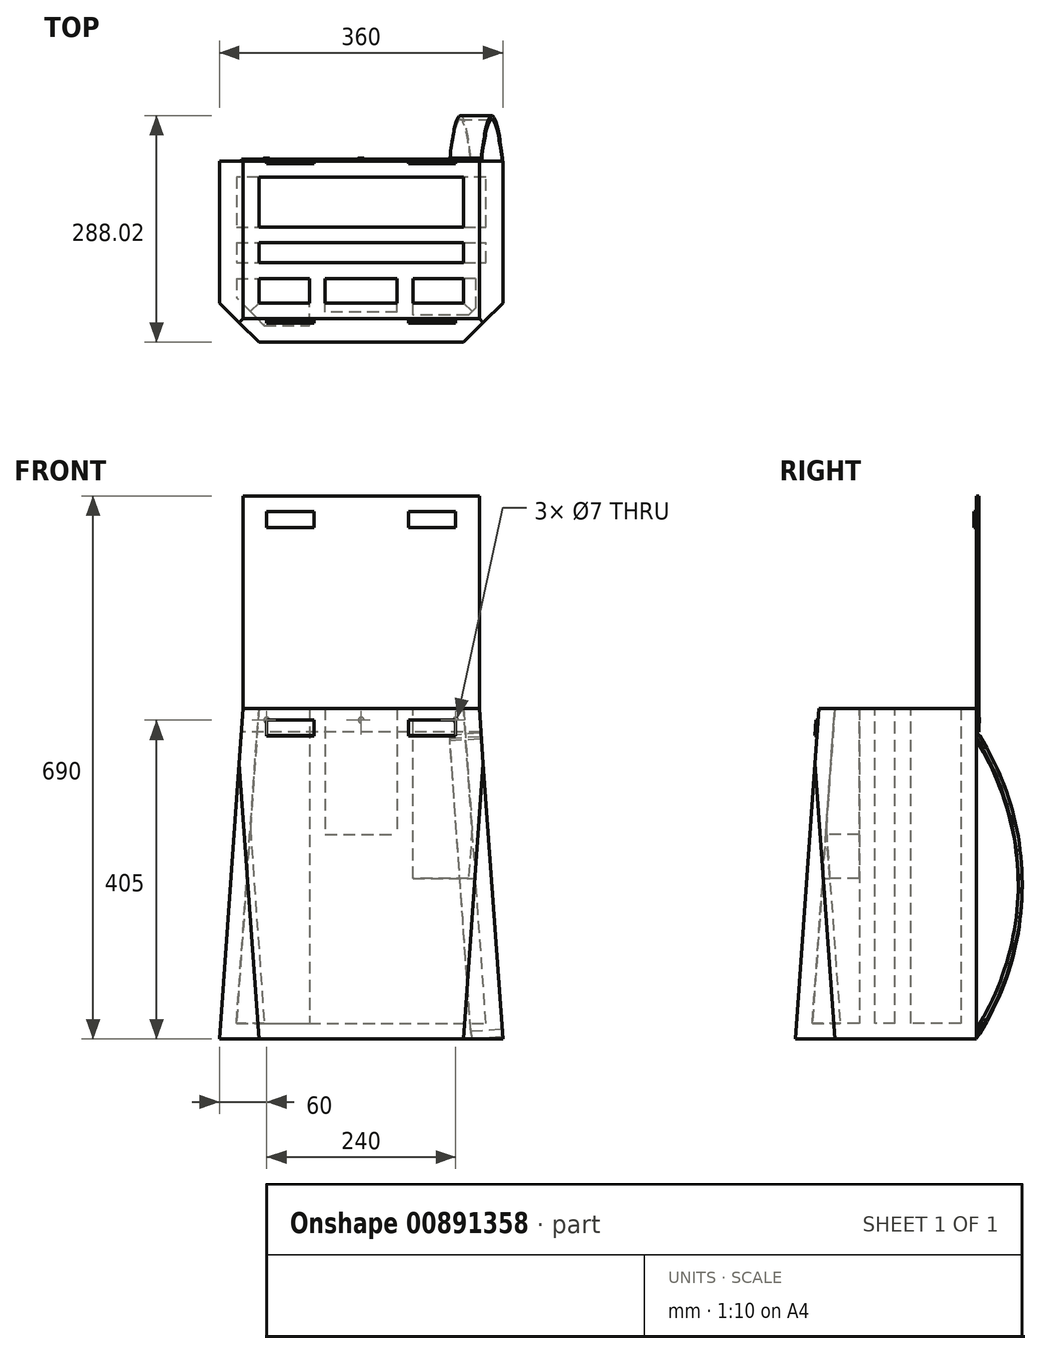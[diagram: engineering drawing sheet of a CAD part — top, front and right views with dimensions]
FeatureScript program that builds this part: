
annotation { "Feature Type Name" : "Feature", "Feature Type Description" : "" }
export const myFeature = defineFeature(function(context is Context, id is Id, definition is map)
    precondition{}
    {
        {
            var Q0;
            Q0=qCreatedBy(makeId("Top.planeOp"),FACE);
            var sketch = newSketch(context, id + "F0", { "sketchPlane" : qUnion([Q0])});
            skLineSegment(sketch, "E0.bottom", {"start": v(150, 100) * mm, "end": v(-150, 100) * mm});
            skLineSegment(sketch, "E0.top", {"start": v(150, -100) * mm, "end": v(-150, -100) * mm});
            skLineSegment(sketch, "E0.left", {"start": v(150, 100) * mm, "end": v(150, -100) * mm});
            skLineSegment(sketch, "E0.right", {"start": v(-150, 100) * mm, "end": v(-150, -100) * mm});
            skPoint(sketch, "E0.middle", {"position": v(0, 0) * mm});
            skSolve(sketch);
        }
        {
            var Q0;
            Q0 = qSketchRegion(id + "F0", true);
            extrude(context, id + "F1", {"entities" : qUnion([Q0]), "depth" : 420 * mm, "offsetDistance" : 25 * mm});
        }
        {
            var Q0;
            Q0=makeQuery(id+"F1.opExtrude","CAP_FACE",FACE,{"disambiguationData":[OSD([sQuery(id+"F0.wireOp",EDGE,"E0.bottom"),sQuery(id+"F0.wireOp",EDGE,"E0.top"),sQuery(id+"F0.wireOp",EDGE,"E0.left"),sQuery(id+"F0.wireOp",EDGE,"E0.right")])],"isStart":true});
            var sketch = newSketch(context, id + "F2", { "sketchPlane" : qUnion([Q0])});
            skLineSegment(sketch, "E1", {"start": v(-150, -100) * mm, "end": v(-180, -100) * mm});
            skLineSegment(sketch, "E2", {"start": v(180, 130) * mm, "end": v(180, -100) * mm});
            skLineSegment(sketch, "E3", {"start": v(180, -100) * mm, "end": v(150, -100) * mm});
            skLineSegment(sketch, "E4", {"start": v(-180, -100) * mm, "end": v(-180, 130) * mm});
            skLineSegment(sketch, "E5", {"start": v(-180, 130) * mm, "end": v(180, 130) * mm});
            skSolve(sketch);
        }
        {
            var Q0;
            Q0=makeQuery(id+"F2.imprint","IMPRINT",FACE,{"disambiguationData":[TD([[makeQuery(id+"F2.imprint","IMPRINT",EDGE,{"derivedFrom":sQuery(id+"F2.wireOp",EDGE,"E1")}),-1.0]])]});
            extrude(context, id + "F3", {"entities" : qUnion([Q0]), "operationType" : NewBodyOperationType.ADD, "oppositeDirection" : true, "depth" : 420 * mm, "offsetDistance" : 25 * mm});
        }
        {
            var Q0;
            Q0=makeQuery(id+"F3.opExtrude","SWEPT_FACE",FACE,{"disambiguationData":[OSD([sQuery(id+"F2.wireOp",EDGE,"E2")])]});
            var sketch = newSketch(context, id + "F4", { "sketchPlane" : qUnion([Q0])});
            skLineSegment(sketch, "E6", {"start": v(-100, 420) * mm, "end": v(-130, 0) * mm});
            skSolve(sketch);
        }
        {
            var Q0;
            {var subQ0=sQuery(id+"F4.wireOp",EDGE,"E6");Q0=makeQuery(id+"F4.imprint","IMPRINT",FACE,{"disambiguationData":[TD([[makeQuery(id+"F4.imprint","IMPRINT",EDGE,{"derivedFrom":subQ0}),-1.0]])]});}
            extrude(context, id + "F5", {"entities" : qUnion([Q0]), "operationType" : NewBodyOperationType.REMOVE, "endBound" : BoundingType.UP_TO_NEXT, "oppositeDirection" : true, "depth" : 25 * mm, "offsetDistance" : 25 * mm});
        }
        {
            var Q0;
            Q0=makeQuery(id+"F3.boolean.opBoolean","MERGE",FACE,{"derivedFrom":[makeQuery(id+"F1.opExtrude","SWEPT_FACE",FACE,{"disambiguationData":[OSD([sQuery(id+"F0.wireOp",EDGE,"E0.bottom")])]}),makeQuery(id+"F3.opExtrude","SWEPT_FACE",FACE,{"disambiguationData":[OSD([sQuery(id+"F2.wireOp",EDGE,"E1")])]}),makeQuery(id+"F3.opExtrude","SWEPT_FACE",FACE,{"disambiguationData":[OSD([sQuery(id+"F2.wireOp",EDGE,"E3")])]})]});
            var sketch = newSketch(context, id + "F6", { "sketchPlane" : qUnion([Q0])});
            skLineSegment(sketch, "E7", {"start": v(-150, 420) * mm, "end": v(-180, 0) * mm});
            skLineSegment(sketch, "E8", {"start": v(150, 420) * mm, "end": v(180, 0) * mm});
            skSolve(sketch);
        }
        {
            var Q0;
            Q0 = qSketchRegion(id + "F6", true);
            var Q1;
            {var subQ0=sQuery(id+"F6.wireOp",EDGE,"E7");Q1=makeQuery(id+"F6.imprint","IMPRINT",FACE,{"disambiguationData":[TD([[makeQuery(id+"F6.imprint","IMPRINT",EDGE,{"derivedFrom":subQ0}),-1.0]])]});}
            var Q2;
            {var subQ0=sQuery(id+"F6.wireOp",EDGE,"E8");Q2=makeQuery(id+"F6.imprint","IMPRINT",FACE,{"disambiguationData":[TD([[makeQuery(id+"F6.imprint","IMPRINT",EDGE,{"derivedFrom":subQ0}),1.0]])]});}
            extrude(context, id + "F7", {"entities" : qUnion([Q0, Q1, Q2]), "operationType" : NewBodyOperationType.REMOVE, "endBound" : BoundingType.UP_TO_NEXT, "oppositeDirection" : true, "depth" : 25 * mm, "offsetDistance" : 25 * mm});
        }
        {
            var Q0;
            {var subQ0=sQuery(id+"F0.wireOp",EDGE,"E0.right");var subQ1=sQuery(id+"F0.wireOp",EDGE,"E0.left");var subQ2=sQuery(id+"F0.wireOp",EDGE,"E0.top");Q0=makeQuery(id+"F3.boolean.opBoolean","MERGE",FACE,{"derivedFrom":[makeQuery(id+"F1.opExtrude","CAP_FACE",FACE,{"disambiguationData":[OSD([sQuery(id+"F0.wireOp",EDGE,"E0.bottom"),subQ2,subQ1,subQ0])],"isStart":true}),makeQuery(id+"F3.opExtrude","CAP_FACE",FACE,{"disambiguationData":[OSD([subQ2,subQ1,subQ0,sQuery(id+"F2.wireOp",EDGE,"E1"),sQuery(id+"F2.wireOp",EDGE,"E2"),sQuery(id+"F2.wireOp",EDGE,"E3"),sQuery(id+"F2.wireOp",EDGE,"E4"),sQuery(id+"F2.wireOp",EDGE,"E5")])],"isStart":true})]});}
            var sketch = newSketch(context, id + "F8", { "sketchPlane" : qUnion([Q0])});
            skLineSegment(sketch, "E9", {"start": v(-130, 130) * mm, "end": v(-180, 80) * mm});
            skLineSegment(sketch, "E10", {"start": v(130, 130) * mm, "end": v(180, 80) * mm});
            skSolve(sketch);
        }
        {
            var Q0;
            Q0 = qSketchRegion(id + "F8", true);
            var Q1;
            {var subQ0=sQuery(id+"F8.wireOp",EDGE,"E9");Q1=makeQuery(id+"F8.imprint","IMPRINT",FACE,{"disambiguationData":[TD([[makeQuery(id+"F8.imprint","IMPRINT",EDGE,{"derivedFrom":subQ0}),-1.0]])]});}
            var Q2;
            {var subQ0=sQuery(id+"F8.wireOp",EDGE,"E10");Q2=makeQuery(id+"F8.imprint","IMPRINT",FACE,{"disambiguationData":[TD([[makeQuery(id+"F8.imprint","IMPRINT",EDGE,{"derivedFrom":subQ0}),1.0]])]});}
            extrude(context, id + "F9", {"entities" : qUnion([Q0, Q1, Q2]), "operationType" : NewBodyOperationType.REMOVE, "oppositeDirection" : true, "depth" : 1000 * mm, "offsetDistance" : 25 * mm});
        }
        {
            var Q0;
            {var subQ0=sQuery(id+"F0.wireOp",EDGE,"E0.right");var subQ1=sQuery(id+"F0.wireOp",EDGE,"E0.left");var subQ2=sQuery(id+"F0.wireOp",EDGE,"E0.top");Q0=makeQuery(id+"F3.boolean.opBoolean","MERGE",FACE,{"derivedFrom":[makeQuery(id+"F1.opExtrude","CAP_FACE",FACE,{"disambiguationData":[OSD([sQuery(id+"F0.wireOp",EDGE,"E0.bottom"),subQ2,subQ1,subQ0])],"isStart":false}),makeQuery(id+"F3.opExtrude","CAP_FACE",FACE,{"disambiguationData":[OSD([subQ2,subQ1,subQ0,sQuery(id+"F2.wireOp",EDGE,"E1"),sQuery(id+"F2.wireOp",EDGE,"E2"),sQuery(id+"F2.wireOp",EDGE,"E3"),sQuery(id+"F2.wireOp",EDGE,"E4"),sQuery(id+"F2.wireOp",EDGE,"E5")])],"isStart":false})]});}
            shell(context, id + "F10", {"entities" : qUnion([Q0]), "thickness" : 20 * mm});
        }
        {
            var Q0;
            Q0=makeQuery(id+"F10.opShell","OFFSET_FACE",FACE,{"disambiguationData":[OSD([sQuery(id+"F0.wireOp",EDGE,"E0.bottom"),sQuery(id+"F0.wireOp",EDGE,"E0.top"),sQuery(id+"F0.wireOp",EDGE,"E0.left"),sQuery(id+"F0.wireOp",EDGE,"E0.right"),sQuery(id+"F2.wireOp",EDGE,"E1"),sQuery(id+"F2.wireOp",EDGE,"E2"),sQuery(id+"F2.wireOp",EDGE,"E3"),sQuery(id+"F2.wireOp",EDGE,"E4"),sQuery(id+"F2.wireOp",EDGE,"E5")])]});
            var sketch = newSketch(context, id + "F11", { "sketchPlane" : qUnion([Q0])});
            skLineSegment(sketch, "E11.bottom", {"start": v(-158.52, 80) * mm, "end": v(158.52, 80) * mm});
            skLineSegment(sketch, "E11.top", {"start": v(-158.52, 16.5) * mm, "end": v(158.52, 16.5) * mm});
            skLineSegment(sketch, "E11.left", {"start": v(-158.52, 80) * mm, "end": v(-158.52, 16.5) * mm});
            skLineSegment(sketch, "E11.right", {"start": v(158.52, 80) * mm, "end": v(158.52, 16.5) * mm});
            skLineSegment(sketch, "E12.bottom", {"start": v(-158.52, -3.5) * mm, "end": v(158.52, -3.5) * mm});
            skLineSegment(sketch, "E12.top", {"start": v(-158.52, -28.9) * mm, "end": v(158.52, -28.9) * mm});
            skLineSegment(sketch, "E12.left", {"start": v(-158.52, -3.5) * mm, "end": v(-158.52, -28.9) * mm});
            skLineSegment(sketch, "E12.right", {"start": v(158.52, -3.5) * mm, "end": v(158.52, -28.9) * mm});
            skLineSegment(sketch, "E13", {"start": v(-65.62, -48.9) * mm, "end": v(-65.62, -83.52) * mm});
            skLineSegment(sketch, "E14", {"start": v(65.62, -48.9) * mm, "end": v(65.62, -83.52) * mm});
            skPoint(sketch, "E14.endSnap0", {"position": v(0, -108.52) * mm});
            skLineSegment(sketch, "E15", {"start": v(-158.52, -48.9) * mm, "end": v(158.52, -48.9) * mm});
            skLineSegment(sketch, "E16", {"start": v(158.52, -48.9) * mm, "end": v(158.52, -83.52) * mm});
            skLineSegment(sketch, "E17", {"start": v(45.62, -48.9) * mm, "end": v(45.62, -83.52) * mm});
            skLineSegment(sketch, "E18", {"start": v(-45.62, -48.9) * mm, "end": v(-45.62, -83.52) * mm});
            skPoint(sketch, "E19.orphan", {"position": v(65.62, -108.52) * mm});
            skLineSegment(sketch, "E20", {"start": v(-45.62, -83.52) * mm, "end": v(-45.62, -108.52) * mm});
            skLineSegment(sketch, "E21", {"start": v(-65.62, -83.52) * mm, "end": v(-65.62, -108.52) * mm});
            skLineSegment(sketch, "E22", {"start": v(45.62, -83.52) * mm, "end": v(45.62, -108.52) * mm});
            skLineSegment(sketch, "E23", {"start": v(45.62, -108.52) * mm, "end": v(46.06, -113.28) * mm});
            skLineSegment(sketch, "E24", {"start": v(65.62, -83.52) * mm, "end": v(65.62, -108.52) * mm});
            skSolve(sketch);
        }
        {
            var Q0;
            {var subQ0=sQuery(id+"F11.wireOp",EDGE,"E11.top");Q0=makeQuery(id+"F11.imprint","IMPRINT",FACE,{"disambiguationData":[TD([[makeQuery(id+"F11.imprint","IMPRINT",EDGE,{"derivedFrom":subQ0}),-1.0]])]});}
            extrude(context, id + "F12", {"entities" : qUnion([Q0]), "operationType" : NewBodyOperationType.ADD, "depth" : 400 * mm, "offsetDistance" : 25 * mm});
        }
        {
            var Q0;
            {var subQ0=sQuery(id+"F11.wireOp",EDGE,"E12.bottom");var subQ1=sQuery(id+"F6.wireOp",EDGE,"E8");Q0=makeQuery(id+"F12.boolean.opBoolean","SPLIT",FACE,{"disambiguationData":[TD([makeQuery(id+"F7.boolean.opBoolean","COPY",FACE,{"derivedFrom":makeQuery(id+"F7.opExtrude","SWEPT_FACE",FACE,{"disambiguationData":[OSD([subQ1])]})})])],"derivedFrom":makeQuery(id+"F12.opExtrude","SWEPT_FACE",FACE,{"disambiguationData":[OSD([subQ0])]})});}
            extrude(context, id + "F13", {"entities" : qUnion([Q0]), "operationType" : NewBodyOperationType.REMOVE, "oppositeDirection" : true, "depth" : 25 * mm, "offsetDistance" : 25 * mm});
        }
        {
            var Q0;
            {var subQ0=sQuery(id+"F11.wireOp",EDGE,"E12.bottom");Q0=makeQuery(id+"F12.boolean.opBoolean","SPLIT",FACE,{"disambiguationData":[TD([makeQuery(id+"F7.boolean.opBoolean","COPY",FACE,{"derivedFrom":makeQuery(id+"F7.opExtrude","SWEPT_FACE",FACE,{"disambiguationData":[OSD([sQuery(id+"F6.wireOp",EDGE,"E7")])]})})])],"derivedFrom":makeQuery(id+"F12.opExtrude","SWEPT_FACE",FACE,{"disambiguationData":[OSD([subQ0])]})});}
            extrude(context, id + "F14", {"entities" : qUnion([Q0]), "operationType" : NewBodyOperationType.REMOVE, "oppositeDirection" : true, "depth" : 25 * mm, "offsetDistance" : 25 * mm});
        }
        {
            var Q0;
            {var subQ7=sQuery(id+"F11.wireOp",EDGE,"E12.top");Q0=makeQuery(id+"F11.imprint","IMPRINT",FACE,{"disambiguationData":[TD([[makeQuery(id+"F11.imprint","IMPRINT",EDGE,{"derivedFrom":subQ7}),-1.0]])]});}
            extrude(context, id + "F15", {"entities" : qUnion([Q0]), "operationType" : NewBodyOperationType.ADD, "depth" : 400 * mm, "offsetDistance" : 25 * mm});
        }
        {
            var Q0;
            {var subQ0=sQuery(id+"F11.wireOp",EDGE,"E13");Q0=makeQuery(id+"F11.imprint","IMPRINT",FACE,{"disambiguationData":[TD([[makeQuery(id+"F11.imprint","IMPRINT",EDGE,{"derivedFrom":subQ0}),1.0]])]});}
            var Q1;
            {var subQ0=sQuery(id+"F11.wireOp",EDGE,"E14");Q1=makeQuery(id+"F11.imprint","IMPRINT",FACE,{"disambiguationData":[TD([[makeQuery(id+"F11.imprint","IMPRINT",EDGE,{"derivedFrom":subQ0}),-1.0]])]});}
            extrude(context, id + "F16", {"entities" : qUnion([Q0, Q1]), "operationType" : NewBodyOperationType.ADD, "depth" : 400 * mm, "offsetDistance" : 25 * mm});
        }
        {
            var Q0;
            {var subQ0=sQuery(id+"F6.wireOp",EDGE,"E8");var subQ11=sQuery(id+"F11.wireOp",EDGE,"E15");Q0=makeQuery(id+"F15.boolean.opBoolean","SPLIT",FACE,{"disambiguationData":[TD([makeQuery(id+"F7.boolean.opBoolean","COPY",FACE,{"derivedFrom":makeQuery(id+"F7.opExtrude","SWEPT_FACE",FACE,{"disambiguationData":[OSD([subQ0])]})})])],"derivedFrom":makeQuery(id+"F15.opExtrude","SWEPT_FACE",FACE,{"disambiguationData":[OSD([subQ11])]})});}
            var Q1;
            {var subQ11=sQuery(id+"F11.wireOp",EDGE,"E15");Q1=makeQuery(id+"F15.boolean.opBoolean","SPLIT",FACE,{"disambiguationData":[TD([makeQuery(id+"F7.boolean.opBoolean","COPY",FACE,{"derivedFrom":makeQuery(id+"F7.opExtrude","SWEPT_FACE",FACE,{"disambiguationData":[OSD([sQuery(id+"F6.wireOp",EDGE,"E7")])]})})])],"derivedFrom":makeQuery(id+"F15.opExtrude","SWEPT_FACE",FACE,{"disambiguationData":[OSD([subQ11])]})});}
            extrude(context, id + "F17", {"entities" : qUnion([Q0, Q1]), "operationType" : NewBodyOperationType.REMOVE, "oppositeDirection" : true, "depth" : 25 * mm, "offsetDistance" : 25 * mm});
        }
        {
            var Q0;
            {var subQ1=sQuery(id+"F4.wireOp",EDGE,"E6");var subQ12=sQuery(id+"F11.wireOp",EDGE,"E21");var subQ14=sQuery(id+"F11.wireOp",EDGE,"E13");Q0=makeQuery(id+"F16.boolean.opBoolean","SPLIT",FACE,{"disambiguationData":[TD([makeQuery(id+"F5.boolean.opBoolean","COPY",FACE,{"derivedFrom":makeQuery(id+"F5.opExtrude","SWEPT_FACE",FACE,{"disambiguationData":[OSD([subQ1])]})})])],"derivedFrom":makeQuery(id+"F16.opExtrude","SWEPT_FACE",FACE,{"disambiguationData":[OSD([subQ14,subQ12])]})});}
            var Q1;
            {var subQ1=sQuery(id+"F4.wireOp",EDGE,"E6");var subQ11=sQuery(id+"F11.wireOp",EDGE,"E22");var subQ14=sQuery(id+"F11.wireOp",EDGE,"E17");Q1=makeQuery(id+"F16.boolean.opBoolean","SPLIT",FACE,{"disambiguationData":[TD([makeQuery(id+"F5.boolean.opBoolean","COPY",FACE,{"derivedFrom":makeQuery(id+"F5.opExtrude","SWEPT_FACE",FACE,{"disambiguationData":[OSD([subQ1])]})})])],"derivedFrom":makeQuery(id+"F16.opExtrude","SWEPT_FACE",FACE,{"disambiguationData":[OSD([subQ14,subQ11])]})});}
            extrude(context, id + "F18", {"entities" : qUnion([Q0, Q1]), "operationType" : NewBodyOperationType.REMOVE, "oppositeDirection" : true, "depth" : 25 * mm, "offsetDistance" : 25 * mm});
        }
        {
            var Q0;
            {var subQ8=sQuery(id+"F11.wireOp",EDGE,"E14");Q0=makeQuery(id+"F11.imprint","IMPRINT",FACE,{"disambiguationData":[TD([[makeQuery(id+"F11.imprint","IMPRINT",EDGE,{"derivedFrom":subQ8}),1.0]])]});}
            extrude(context, id + "F19", {"entities" : qUnion([Q0]), "operationType" : NewBodyOperationType.ADD, "depth" : 184.1 * mm, "offsetDistance" : 25 * mm});
        }
        {
            var Q0;
            {var subQ1=sQuery(id+"F11.wireOp",EDGE,"E17");Q0=makeQuery(id+"F11.imprint","IMPRINT",FACE,{"disambiguationData":[TD([[makeQuery(id+"F11.imprint","IMPRINT",EDGE,{"derivedFrom":subQ1}),-1.0]])]});}
            extrude(context, id + "F20", {"entities" : qUnion([Q0]), "operationType" : NewBodyOperationType.ADD, "depth" : 240 * mm, "offsetDistance" : 25 * mm});
        }
        {
            var Q0;
            {var subQ0=sQuery(id+"F4.wireOp",EDGE,"E6");Q0=makeQuery(id+"F18.boolean.opBoolean","MERGE",FACE,{"derivedFrom":[makeQuery(id+"F5.boolean.opBoolean","COPY",FACE,{"derivedFrom":makeQuery(id+"F5.opExtrude","SWEPT_FACE",FACE,{"disambiguationData":[OSD([subQ0])]})})],"fromTools":[makeQuery(id+"F18.opExtrude","SWEPT_FACE",FACE,{"disambiguationData":[OSD([subQ0,sQuery(id+"F11.wireOp",EDGE,"E13"),sQuery(id+"F11.wireOp",EDGE,"E21")])]}),makeQuery(id+"F18.opExtrude","SWEPT_FACE",FACE,{"disambiguationData":[OSD([subQ0,sQuery(id+"F11.wireOp",EDGE,"E17"),sQuery(id+"F11.wireOp",EDGE,"E22")])]})]});}
            var sketch = newSketch(context, id + "F21", { "sketchPlane" : qUnion([Q0])});
            skLineSegment(sketch, "E25", {"start": v(-150, 411.8) * mm, "end": v(-155, 341.63) * mm});
            skLineSegment(sketch, "E26", {"start": v(-155, 341.63) * mm, "end": v(155, 341.63) * mm});
            skLineSegment(sketch, "E27", {"start": v(155, 341.63) * mm, "end": v(150, 411.8) * mm});
            skLineSegment(sketch, "E28", {"start": v(150, 411.8) * mm, "end": v(-150, 411.8) * mm});
            skLineSegment(sketch, "E29.bottom", {"start": v(-120, 396.8) * mm, "end": v(-60, 396.8) * mm});
            skLineSegment(sketch, "E29.top", {"start": v(-120, 376.8) * mm, "end": v(-60, 376.8) * mm});
            skLineSegment(sketch, "E29.left", {"start": v(-120, 396.8) * mm, "end": v(-120, 376.8) * mm});
            skLineSegment(sketch, "E29.right", {"start": v(-60, 396.8) * mm, "end": v(-60, 376.8) * mm});
            skLineSegment(sketch, "E30.bottom", {"start": v(60, 396.8) * mm, "end": v(120, 396.8) * mm});
            skLineSegment(sketch, "E30.top", {"start": v(60, 376.8) * mm, "end": v(120, 376.8) * mm});
            skLineSegment(sketch, "E30.left", {"start": v(60, 396.8) * mm, "end": v(60, 376.8) * mm});
            skLineSegment(sketch, "E30.right", {"start": v(120, 396.8) * mm, "end": v(120, 376.8) * mm});
            skLineSegment(sketch, "E31", {"start": v(-155, 341.63) * mm, "end": v(-130, -9.26) * mm});
            skLineSegment(sketch, "E32", {"start": v(-130, -9.26) * mm, "end": v(130, -9.26) * mm});
            skLineSegment(sketch, "E33", {"start": v(130, -9.26) * mm, "end": v(155, 341.63) * mm});
            skSolve(sketch);
        }
        {
            var Q0;
            Q0=makeQuery(id+"F3.boolean.opBoolean","MERGE",FACE,{"derivedFrom":[makeQuery(id+"F1.opExtrude","SWEPT_FACE",FACE,{"disambiguationData":[OSD([sQuery(id+"F0.wireOp",EDGE,"E0.bottom")])]}),makeQuery(id+"F3.opExtrude","SWEPT_FACE",FACE,{"disambiguationData":[OSD([sQuery(id+"F2.wireOp",EDGE,"E1")])]}),makeQuery(id+"F3.opExtrude","SWEPT_FACE",FACE,{"disambiguationData":[OSD([sQuery(id+"F2.wireOp",EDGE,"E3")])]})]});
            var sketch = newSketch(context, id + "F22", { "sketchPlane" : qUnion([Q0])});
            skLineSegment(sketch, "E34", {"start": v(-152.14, 390) * mm, "end": v(152.14, 390) * mm});
            skLineSegment(sketch, "E35", {"start": v(152.14, 390) * mm, "end": v(150, 420) * mm});
            skLineSegment(sketch, "E36", {"start": v(150, 420) * mm, "end": v(-150, 420) * mm});
            skLineSegment(sketch, "E37", {"start": v(-150, 420) * mm, "end": v(-152.14, 390) * mm});
            skLineSegment(sketch, "E38", {"start": v(-150, 420) * mm, "end": v(-150, 620) * mm});
            skLineSegment(sketch, "E39", {"start": v(-150, 620) * mm, "end": v(150, 620) * mm});
            skLineSegment(sketch, "E40", {"start": v(150, 620) * mm, "end": v(150, 420) * mm});
            skLineSegment(sketch, "E41.left", {"start": v(-150, 620) * mm, "end": v(-150, 620) * mm});
            skLineSegment(sketch, "E41.right", {"start": v(150, 620) * mm, "end": v(150, 620) * mm});
            skLineSegment(sketch, "E42", {"start": v(-150, 620) * mm, "end": v(-150, 690) * mm});
            skLineSegment(sketch, "E43", {"start": v(-150, 690) * mm, "end": v(150, 690) * mm});
            skLineSegment(sketch, "E44", {"start": v(150, 690) * mm, "end": v(150, 620) * mm});
            skLineSegment(sketch, "E45.bottom", {"start": v(120, 670) * mm, "end": v(60, 670) * mm});
            skLineSegment(sketch, "E45.top", {"start": v(120, 650) * mm, "end": v(60, 650) * mm});
            skLineSegment(sketch, "E45.left", {"start": v(120, 670) * mm, "end": v(120, 650) * mm});
            skLineSegment(sketch, "E45.right", {"start": v(60, 670) * mm, "end": v(60, 650) * mm});
            skLineSegment(sketch, "E46.bottom", {"start": v(-60, 670) * mm, "end": v(-120, 670) * mm});
            skLineSegment(sketch, "E46.top", {"start": v(-60, 650) * mm, "end": v(-120, 650) * mm});
            skLineSegment(sketch, "E46.left", {"start": v(-60, 670) * mm, "end": v(-60, 650) * mm});
            skLineSegment(sketch, "E46.right", {"start": v(-120, 670) * mm, "end": v(-120, 650) * mm});
            skCircle(sketch, "E47", {"center": v(-120, 405) * mm, "radius": 3.5 * mm});
            skCircle(sketch, "E48", {"center": v(0, 405) * mm, "radius": 3.5 * mm});
            skCircle(sketch, "E49", {"center": v(120, 405) * mm, "radius": 3.5 * mm});
            skSolve(sketch);
        }
        {
            var Q0;
            Q0=makeQuery(id+"F22.imprint","IMPRINT",FACE,{"disambiguationData":[TD([[makeQuery(id+"F22.imprint","IMPRINT",EDGE,{"derivedFrom":sQuery(id+"F22.wireOp",EDGE,"E36")}),1.0]])]});
            var Q1;
            Q1=makeQuery(id+"F22.imprint","IMPRINT",FACE,{"disambiguationData":[TD([[makeQuery(id+"F22.imprint","IMPRINT",EDGE,{"derivedFrom":sQuery(id+"F22.wireOp",EDGE,"E34")}),1.0]])]});
            var Q2;
            Q2=makeQuery(id+"F22.imprint","IMPRINT",FACE,{"disambiguationData":[TD([[makeQuery(id+"F22.imprint","IMPRINT",EDGE,{"derivedFrom":sQuery(id+"F22.wireOp",EDGE,"E39")}),1.0]])]});
            var Q3;
            Q3=makeQuery(id+"F22.imprint","IMPRINT",FACE,{"disambiguationData":[TD([[makeQuery(id+"F22.imprint","IMPRINT",EDGE,{"derivedFrom":sQuery(id+"F22.wireOp",EDGE,"E46.bottom")}),1.0]])]});
            var Q4;
            Q4=makeQuery(id+"F22.imprint","IMPRINT",FACE,{"disambiguationData":[TD([[makeQuery(id+"F22.imprint","IMPRINT",EDGE,{"derivedFrom":sQuery(id+"F22.wireOp",EDGE,"E45.bottom")}),1.0]])]});
            extrude(context, id + "F23", {"entities" : qUnion([Q0, Q1, Q2, Q3, Q4]), "depth" : 3 * mm, "offsetDistance" : 25 * mm});
        }
        {
            var Q0;
            Q0=makeQuery(id+"F22.imprint","IMPRINT",FACE,{"disambiguationData":[TD([[makeQuery(id+"F22.imprint","IMPRINT",EDGE,{"derivedFrom":sQuery(id+"F22.wireOp",EDGE,"E45.bottom")}),1.0]])]});
            var Q1;
            Q1=makeQuery(id+"F22.imprint","IMPRINT",FACE,{"disambiguationData":[TD([[makeQuery(id+"F22.imprint","IMPRINT",EDGE,{"derivedFrom":sQuery(id+"F22.wireOp",EDGE,"E46.bottom")}),1.0]])]});
            extrude(context, id + "F24", {"entities" : qUnion([Q0, Q1]), "operationType" : NewBodyOperationType.ADD, "oppositeDirection" : true, "depth" : 3 * mm, "offsetDistance" : 25 * mm});
        }
        {
            var Q0;
            Q0=makeQuery(id+"F21.imprint","IMPRINT",FACE,{"disambiguationData":[TD([[makeQuery(id+"F21.imprint","IMPRINT",EDGE,{"derivedFrom":sQuery(id+"F21.wireOp",EDGE,"E29.bottom")}),-1.0]])]});
            var Q1;
            Q1=makeQuery(id+"F21.imprint","IMPRINT",FACE,{"disambiguationData":[TD([[makeQuery(id+"F21.imprint","IMPRINT",EDGE,{"derivedFrom":sQuery(id+"F21.wireOp",EDGE,"E30.bottom")}),-1.0]])]});
            extrude(context, id + "F25", {"entities" : qUnion([Q0, Q1]), "depth" : 3 * mm, "offsetDistance" : 25 * mm});
        }
        {
            var Q0;
            {var subQ0=sQuery(id+"F11.wireOp",EDGE,"E12.bottom");var subQ1=sQuery(id+"F6.wireOp",EDGE,"E7");Q0=makeQuery(id+"F23.boolean.opBoolean","MERGE",FACE,{"derivedFrom":[makeQuery(id+"F17.boolean.opBoolean","MERGE",FACE,{"derivedFrom":[makeQuery(id+"F14.boolean.opBoolean","MERGE",FACE,{"derivedFrom":[makeQuery(id+"F7.boolean.opBoolean","COPY",FACE,{"derivedFrom":makeQuery(id+"F7.opExtrude","SWEPT_FACE",FACE,{"disambiguationData":[OSD([subQ1])]})})],"fromTools":[makeQuery(id+"F14.opExtrude","SWEPT_FACE",FACE,{"disambiguationData":[OSD([subQ1,subQ0])]})]})],"fromTools":[makeQuery(id+"F17.opExtrude","SWEPT_FACE",FACE,{"disambiguationData":[OSD([subQ1,subQ0,sQuery(id+"F11.wireOp",EDGE,"E15")])]})]}),makeQuery(id+"F23.opExtrude","SWEPT_FACE",FACE,{"disambiguationData":[OSD([sQuery(id+"F22.wireOp",EDGE,"E37")])]})]});}
            var sketch = newSketch(context, id + "F26", { "sketchPlane" : qUnion([Q0])});
            skArc(sketch, "E50", {"start": v(100, 0) * mm, "mid": v(153.02, 185.05) * mm, "end": v(100, 370.1) * mm});
            skArc(sketch, "E51.0", {"start": v(104.24, -2.65) * mm, "mid": v(158.02, 185.05) * mm, "end": v(104.24, 372.75) * mm});
            skLineSegment(sketch, "E52", {"start": v(104.24, 372.75) * mm, "end": v(100, 377.53) * mm});
            skLineSegment(sketch, "E53", {"start": v(104.24, -2.65) * mm, "end": v(100, -9.44) * mm});
            skLineSegment(sketch, "E54", {"start": v(-100, 408.25) * mm, "end": v(100, 408.25) * mm});
            skLineSegment(sketch, "E55", {"start": v(100, -12.82) * mm, "end": v(-80, -12.82) * mm});
            skLineSegment(sketch, "E56", {"start": v(-80, -12.82) * mm, "end": v(-105, 338.07) * mm});
            skLineSegment(sketch, "E57", {"start": v(-105, 338.07) * mm, "end": v(-100, 408.25) * mm});
            skSolve(sketch);
        }
        {
            var Q0;
            Q0 = qSketchRegion(id + "F26", true);
            var Q1;
            {var subQ1=sQuery(id+"F26.wireOp",EDGE,"E50");Q1=makeQuery(id+"F26.imprint","IMPRINT",FACE,{"disambiguationData":[TD([[makeQuery(id+"F26.imprint","IMPRINT",EDGE,{"derivedFrom":subQ1}),-1.0]])]});}
            extrude(context, id + "F27", {"entities" : qUnion([Q0, Q1]), "oppositeDirection" : true, "depth" : 40 * mm, "offsetDistance" : 25 * mm});
        }
        {
            var Q0;
            Q0=makeQuery(id+"F22.imprint","IMPRINT",FACE,{"disambiguationData":[TD([[makeQuery(id+"F22.imprint","IMPRINT",EDGE,{"derivedFrom":sQuery(id+"F22.wireOp",EDGE,"E47")}),1.0]])]});
            var Q1;
            Q1=makeQuery(id+"F22.imprint","IMPRINT",FACE,{"disambiguationData":[TD([[makeQuery(id+"F22.imprint","IMPRINT",EDGE,{"derivedFrom":sQuery(id+"F22.wireOp",EDGE,"E48")}),1.0]])]});
            var Q2;
            Q2=makeQuery(id+"F22.imprint","IMPRINT",FACE,{"disambiguationData":[TD([[makeQuery(id+"F22.imprint","IMPRINT",EDGE,{"derivedFrom":sQuery(id+"F22.wireOp",EDGE,"E49")}),1.0]])]});
            extrude(context, id + "F28", {"entities" : qUnion([Q0, Q1, Q2]), "depth" : 4 * mm, "offsetDistance" : 25 * mm});
        }
    });
